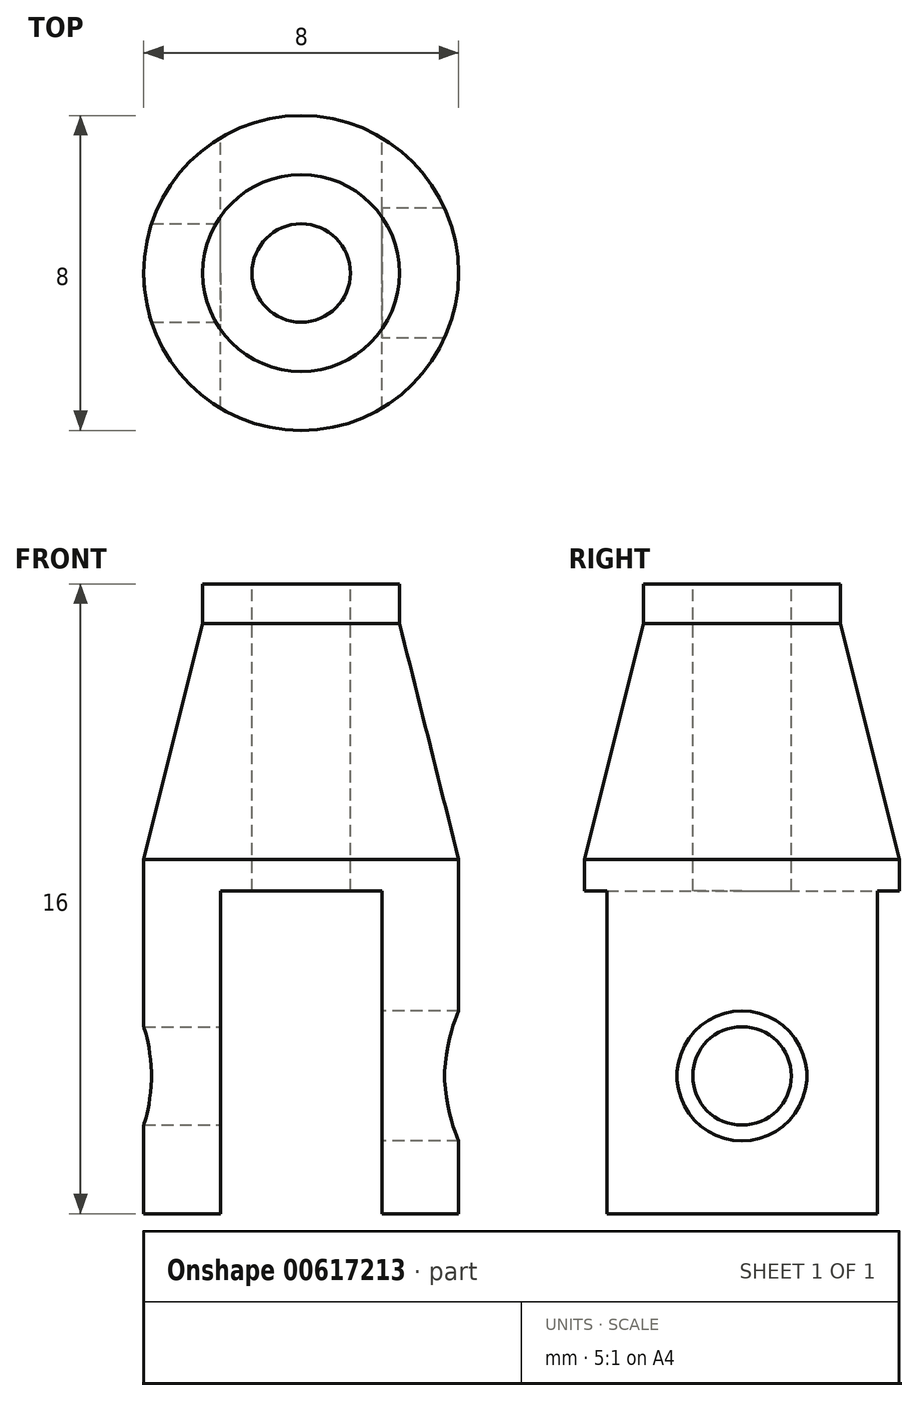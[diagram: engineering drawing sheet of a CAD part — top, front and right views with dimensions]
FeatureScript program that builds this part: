
annotation { "Feature Type Name" : "Feature", "Feature Type Description" : "" }
export const myFeature = defineFeature(function(context is Context, id is Id, definition is map)
    precondition{}
    {
        {
            var Q0;
            Q0=qCreatedBy(makeId("Front.planeOp"),FACE);
            var sketch = newSketch(context, id + "F0", { "sketchPlane" : qUnion([Q0])});
            skLineSegment(sketch, "E0", {"start": v(0, 0) * mm, "end": v(0, -24.07) * mm, "construction": true});
            skLineSegment(sketch, "E1", {"start": v(0, 0) * mm, "end": v(2.5, 0) * mm});
            skLineSegment(sketch, "E2", {"start": v(2.5, 0) * mm, "end": v(2.5, -1) * mm});
            skLineSegment(sketch, "E3", {"start": v(2.5, -1) * mm, "end": v(4, -7) * mm});
            skLineSegment(sketch, "E4", {"start": v(4, -7) * mm, "end": v(4, -16) * mm});
            skLineSegment(sketch, "E5", {"start": v(4, -16) * mm, "end": v(0, -16) * mm});
            skLineSegment(sketch, "E6", {"start": v(0, -16) * mm, "end": v(0, 0) * mm});
            skSolve(sketch);
        }
        {
            var Q0;
            Q0 = qSketchRegion(id + "F0", true);
            var Q1;
            Q1=sQuery(id+"F0.wireOp",EDGE,"E0");
            revolve(context, id + "F1", {"entities" : qUnion([Q0]), "axis" : qUnion([Q1]), "revolveType" : RevolveType.FULL});
        }
        {
            var Q0;
            Q0=qCreatedBy(makeId("Front.planeOp"),FACE);
            var sketch = newSketch(context, id + "F2", { "sketchPlane" : qUnion([Q0])});
            skLineSegment(sketch, "E7.bottom", {"start": v(2.05, -16) * mm, "end": v(-2.05, -16) * mm});
            skLineSegment(sketch, "E7.top", {"start": v(2.05, -7.8) * mm, "end": v(-2.05, -7.8) * mm});
            skLineSegment(sketch, "E7.left", {"start": v(2.05, -16) * mm, "end": v(2.05, -7.8) * mm});
            skLineSegment(sketch, "E7.right", {"start": v(-2.05, -16) * mm, "end": v(-2.05, -7.8) * mm});
            skPoint(sketch, "E7.middle", {"position": v(0, -11.9) * mm});
            skSolve(sketch);
        }
        {
            var Q0;
            Q0 = qSketchRegion(id + "F2", true);
            extrude(context, id + "F3", {"entities" : qUnion([Q0]), "operationType" : NewBodyOperationType.REMOVE, "endBound" : BoundingType.THROUGH_ALL, "depth" : 25 * mm, "offsetDistance" : 25 * mm, "hasSecondDirection" : true, "secondDirectionBound" : SecondDirectionBoundingType.THROUGH_ALL, "secondDirectionOppositeDirection" : true, "secondDirectionDepth" : 25 * mm});
        }
        {
            var Q0;
            Q0=qCreatedBy(makeId("Right.planeOp"),FACE);
            var sketch = newSketch(context, id + "F4", { "sketchPlane" : qUnion([Q0])});
            skLineSegment(sketch, "E8", {"start": v(0, -16) * mm, "end": v(0, -12.5) * mm, "construction": true});
            skSolve(sketch);
        }
        {
            var Q0;
            Q0=sQuery(id+"F4.wireOp",VERTEX,"E8.end");
            var Q1;
            Q1=makeQuery(id+"F1.opRevolve","SWEPT_BODY",BODY,{"disambiguationData":[OSD([sQuery(id+"F0.wireOp",EDGE,"E1"),sQuery(id+"F0.wireOp",EDGE,"E2"),sQuery(id+"F0.wireOp",EDGE,"E3"),sQuery(id+"F0.wireOp",EDGE,"E4"),sQuery(id+"F0.wireOp",EDGE,"E5"),sQuery(id+"F0.wireOp",EDGE,"E6")])]});
            hole(context, id + "F5", {"style" : HoleStyle.SIMPLE, "endStyle" : HoleEndStyle.THROUGH, "oppositeDirection" : true, "standardTappedOrClearance" : lookupTablePath({ "standard" : "ISO", "fit" : "Normal", "size" : "M3", "type" : "Clearance" }), "standardBlindInLast" : lookupTablePath({ "fit" : "Standard", "standard" : "ISO", "size" : "M3", "type" : "Clearance" }), "holeDiameter" : 3.3 * mm, "majorDiameter" : 5 * mm, "isTappedThrough" : true, "tappedDepth" : 6 * mm, "tapClearance" : 2, "locations" : qUnion([Q0]), "scope" : qUnion([Q1])});
        }
        {
            var Q0;
            Q0=sQuery(id+"F4.wireOp",VERTEX,"E8.end");
            var Q1;
            Q1=makeQuery(id+"F1.opRevolve","SWEPT_BODY",BODY,{"disambiguationData":[OSD([sQuery(id+"F0.wireOp",EDGE,"E1"),sQuery(id+"F0.wireOp",EDGE,"E2"),sQuery(id+"F0.wireOp",EDGE,"E3"),sQuery(id+"F0.wireOp",EDGE,"E4"),sQuery(id+"F0.wireOp",EDGE,"E5"),sQuery(id+"F0.wireOp",EDGE,"E6")])]});
            hole(context, id + "F6", {"style" : HoleStyle.SIMPLE, "endStyle" : HoleEndStyle.THROUGH, "standardTappedOrClearance" : lookupTablePath({ "standard" : "ISO", "engagement" : "75%", "pitch" : "0.5 mm", "size" : "M3", "type" : "Tapped" }), "standardBlindInLast" : lookupTablePath({ "standard" : "ISO", "engagement" : "75%", "pitch" : "0.5 mm", "size" : "M3", "type" : "Tapped" }), "holeDiameter" : 2.5 * mm, "majorDiameter" : 3 * mm, "showTappedDepth" : true, "isTappedThrough" : true, "tappedDepth" : 6 * mm, "tapClearance" : 2, "locations" : qUnion([Q0]), "scope" : qUnion([Q1])});
        }
        {
            var Q0;
            Q0=makeQuery(id+"F1.opRevolve","SWEPT_FACE",FACE,{"disambiguationData":[OSD([sQuery(id+"F0.wireOp",EDGE,"E1")])]});
            var sketch = newSketch(context, id + "F7", { "sketchPlane" : qUnion([Q0])});
            skPoint(sketch, "E9", {"position": v(0, 0) * mm});
            skSolve(sketch);
        }
        {
            var Q0;
            Q0=sQuery(id+"F7.wireOp",VERTEX,"E9");
            var Q1;
            Q1=makeQuery(id+"F1.opRevolve","SWEPT_BODY",BODY,{"disambiguationData":[OSD([sQuery(id+"F0.wireOp",EDGE,"E1"),sQuery(id+"F0.wireOp",EDGE,"E2"),sQuery(id+"F0.wireOp",EDGE,"E3"),sQuery(id+"F0.wireOp",EDGE,"E4"),sQuery(id+"F0.wireOp",EDGE,"E5"),sQuery(id+"F0.wireOp",EDGE,"E6")])]});
            hole(context, id + "F8", {"style" : HoleStyle.SIMPLE, "endStyle" : HoleEndStyle.THROUGH, "standardTappedOrClearance" : lookupTablePath({ "standard" : "ISO", "engagement" : "75%", "pitch" : "0.5 mm", "size" : "M3", "type" : "Tapped" }), "standardBlindInLast" : lookupTablePath({ "standard" : "ISO", "engagement" : "75%", "pitch" : "0.5 mm", "size" : "M3", "type" : "Tapped" }), "holeDiameter" : 2.5 * mm, "majorDiameter" : 3 * mm, "showTappedDepth" : true, "isTappedThrough" : true, "tappedDepth" : 6 * mm, "tapClearance" : 2, "locations" : qUnion([Q0]), "scope" : qUnion([Q1])});
        }
    });
